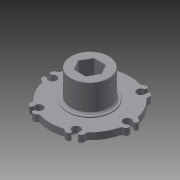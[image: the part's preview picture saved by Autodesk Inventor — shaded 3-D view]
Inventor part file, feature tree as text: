
AUTODESK INVENTOR PART (.ipt)
format: ipt  version: 2014 SP1 (Build 180222100, 222)  size: 317,952 bytes
history: native  units: in
note: dims shown in document units (in); Inventor stores cm internally (conversion verified against a paired STEP export)
features: fillet x1, other x1, imported_body x1
ambient origin geometry x8: Origin, YZ Plane, XZ Plane, XY Plane, X Axis, Y Axis, Z Axis, Center Point
bodies: Body1 (feature_tree)
feature tree (3):
  fillet  "Fillet7"  [1 undecoded]
  other  "am-2568 500EX Hex Hub1"
  imported_body  "Base1"
note: 1 required parameter value undecoded (feature->parameter linkage not recoverable at this tier; creation-order binding heuristic only, values carry confidence <= 0.55)
